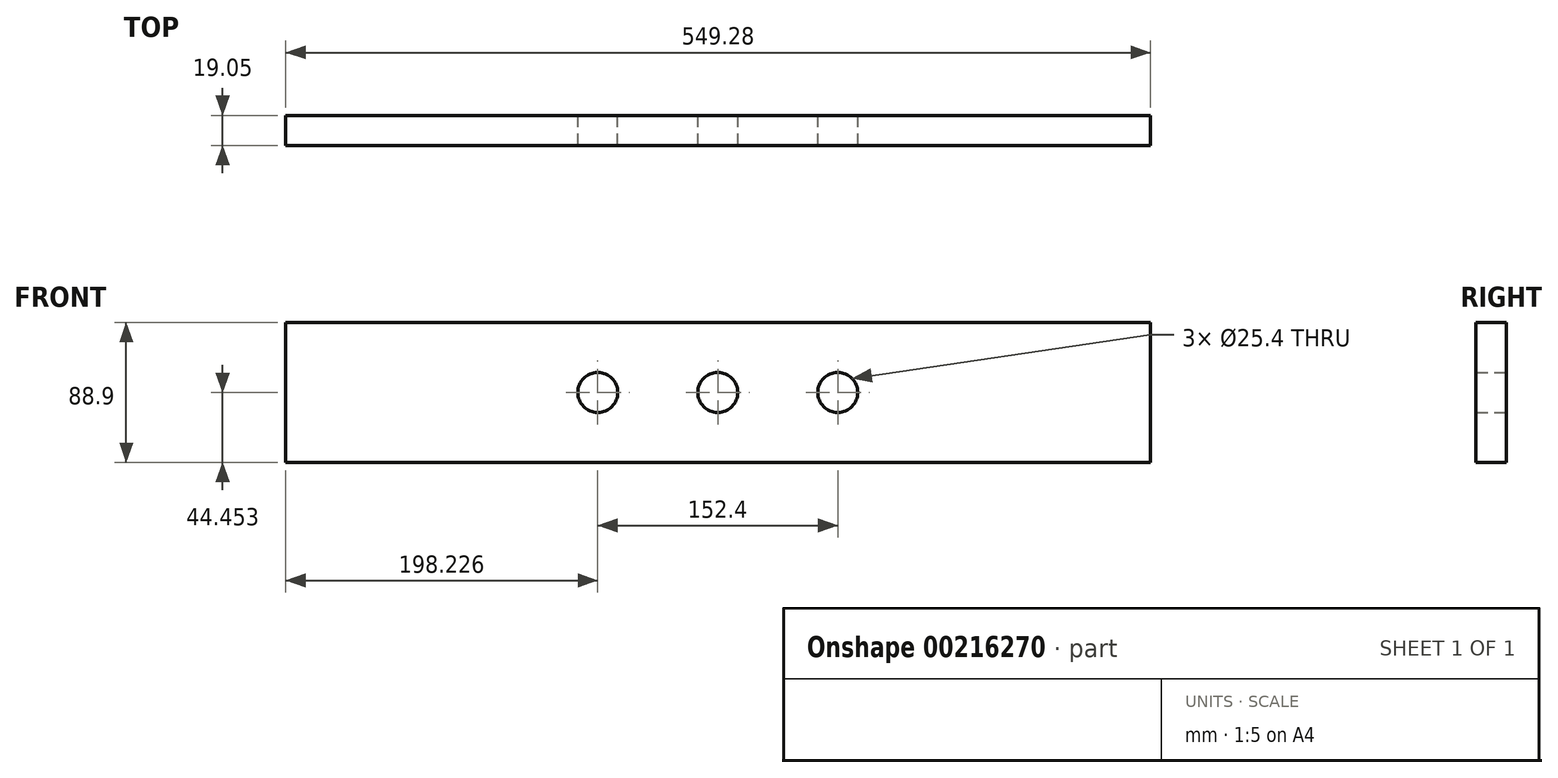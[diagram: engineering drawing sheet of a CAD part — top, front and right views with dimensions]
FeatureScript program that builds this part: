
annotation { "Feature Type Name" : "Feature", "Feature Type Description" : "" }
export const myFeature = defineFeature(function(context is Context, id is Id, definition is map)
    precondition{}
    {
        {
            var Q0;
            Q0=qCreatedBy(makeId("Front.planeOp"),FACE);
            var sketch = newSketch(context, id + "F0", { "sketchPlane" : qUnion([Q0])});
            skLineSegment(sketch, "E0", {"start": v(-1458.24, 75.31) * mm, "end": v(-908.96, 75.31) * mm});
            skLineSegment(sketch, "E1", {"start": v(-908.96, 75.31) * mm, "end": v(-908.96, 164.21) * mm});
            skLineSegment(sketch, "E2", {"start": v(-908.96, 164.21) * mm, "end": v(-1458.24, 164.21) * mm});
            skLineSegment(sketch, "E3", {"start": v(-1458.24, 164.21) * mm, "end": v(-1458.24, 75.31) * mm});
            skCircle(sketch, "E4", {"center": v(-1183.81, 119.76) * mm, "radius": 12.7 * mm});
            skCircle(sketch, "E5", {"center": v(-1107.61, 119.76) * mm, "radius": 12.7 * mm});
            skCircle(sketch, "E6", {"center": v(-1260.01, 119.76) * mm, "radius": 12.7 * mm});
            skLineSegment(sketch, "E7", {"start": v(-1458.24, 119.76) * mm, "end": v(-908.96, 119.76) * mm, "construction": true});
            skSolve(sketch);
        }
        {
            var Q0;
            Q0=makeQuery(id+"F0.imprint","IMPRINT",FACE,{"disambiguationData":[TD([[makeQuery(id+"F0.imprint","IMPRINT",EDGE,{"derivedFrom":sQuery(id+"F0.wireOp",EDGE,"E0")}),1.0]])]});
            extrude(context, id + "F1", {"entities" : qUnion([Q0]), "depth" : 19.05 * mm});
        }
    });
